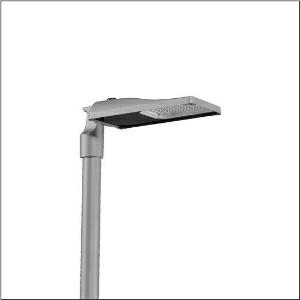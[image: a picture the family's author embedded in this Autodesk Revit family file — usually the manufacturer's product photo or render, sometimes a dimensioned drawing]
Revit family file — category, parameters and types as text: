
# Revit family: streetlight_sl_31_mini___st1_0a_5xh6d3as08ja_952b
name_source: partatom
category: Lighting Fixtures
units: mm (PartAtom-declared; Revit-internal decimal feet)

## family parameters
Cut with Voids When Loaded = No
Host = Face
Light Source = No
Part Type = Normal
Room Calculation Point = No
Round Connector Dimension = Use Diameter
Shared = No

## types (1)
- --- (1 x LED, 12270 lm, 82.5 W, 3000K)
    Apparent Load = 83 VA
    CIE Flux Codes = 40 73 97 100 100
    Color Rendering = 70
    Color Temperature = 3000K
    Default Elevation = 1800 mm
    Description = Streetlight SL 31 mini D4i mast luminaire for post-top, side-entry; light control with lens of PMMA; light distribution: ST1.0a, direct asymmetric distribution, for standard-compliant lighting for roads and squares; LED: luminous flux: 12.270lm, light colour: 730, colour temperature: 3000K; luminous efficacy: 148,7lm/W; control: pre-setting: logarithmic dimming characteristic, flexible luminous flux parameterisation, time-dependent luminous flux control, constant luminous flux control, power reduction, intelligent temperature release in ECG and LED module, overheat protection; luminaire housing, of diecast aluminium, SITECO metallic grey (DB 702S), corrosivity category C5 high according to DIN EN ISO 12944; cover of toughened safety glass, transparent, opened without tools; mast flange of diecast aluminium, SITECO metallic grey (DB 702S), spigot size: 76/60mm, mast flange included unmounted; cable length: 10,5m, connection cable pre-assembled; mains connection: 220..240V, AC, 50/60Hz; power consumption (at start of service life): 82,5W / (at end of service life): 90,1W / (with reduced operation 50%): 36,8W; protection rating (complete): IP66; insulation class (complete): insulation class II (safety insulation); impact resistance: IK10; certification: CE, ENEC, ENEC+, VDE, UKCA, ZD4i; permissible operating ambient temperature for outdoor applications: -40..+50°C; packaging unit: 1 piece

Light Distribution: ST1.0a
    Height = 76 mm
    Lamp = 1 x LED
    Lamp Light Flux = 12270 lm
    Lamp Power = 82.5 W
    Lamp count = 1
    Length = 547 mm
    Luminous efficacy = 149 lm/W
    Manufacturer = Siteco
    ModVariant = No
    Model = 5XH6D3AS08JA
    Number of Poles = 1
    OnlyDefault = Yes
    Power Factor = 1
    Product Name = Streetlight SL 31 mini | ST1.0a
    Product group = mast luminaire | pylon top
    ProductGroupID = 6100
    Protection Class = Protection class II
    Protection Degree = IP 66
    RLX_Detail_Level = 1
    RLX_Emergency_Light_Flux = 0 lm
    RLX_Emergency_Type = 0
    RLX_Emergency_Type_DB = No
    RlxData = <blob elided: 39717 chars, md5=56fff2e7>
    Socket = socket
    Standby Power = 0 W
    System Light Flux = 12270 lm
    System Power = 83 W
    Type Comments = factory setting: luminous flux: 100 % | dim-lin: 254 | 870 mA
    Type Image = l_1300330.jpg
    URL = http://relux.com
    VarID = @adj_057115
    Voltage = 0 V
    Weight = 0.00 kg
    Width = 265 mm

## geometry (parser evidence)
native form markers: Blend x4, Sweep x9
no freeform markers — native parametric forms only
